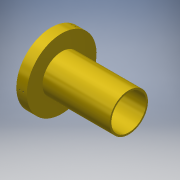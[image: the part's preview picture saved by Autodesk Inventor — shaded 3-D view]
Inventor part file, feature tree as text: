
AUTODESK INVENTOR PART (.ipt)
format: ipt  version: 2017 (Build 210142000, 142)  size: 156,672 bytes
history: native  units: in
note: dims shown in document units (in); Inventor stores cm internally (conversion verified against a paired STEP export)
features: sketch x2, revolve x1, plane x1, hole x1, pattern_circular x1
ambient origin geometry x8: Origin, YZ Plane, XZ Plane, XY Plane, X Axis, Y Axis, Z Axis, Center Point
bodies: Solid1 (feature_tree)
feature tree (6):
  revolve  "Revolution1"  [1 undecoded]
  plane  "Work Plane1"
  hole  "Hole1"  [1 undecoded]
  pattern_circular  "Circular Pattern1"  Count=8  [1 undecoded]
  sketch  "Sketch1"  dims[d0=0.4724in d1=3.5039in]
  sketch  "Sketch2"  dims[d2=1.5748in d3=1.7323in d4=3.1496in d5=90.0deg d6=0.1575in d7=0.0617in d8=0.2362in d9=0.1575in d10=0.0787in d11=90.0deg d12=0.315in d13=0.8108in d14=1.1811in d15=360.0deg]
note: 3 required parameter values undecoded (feature->parameter linkage not recoverable at this tier; creation-order binding heuristic only, values carry confidence <= 0.55)